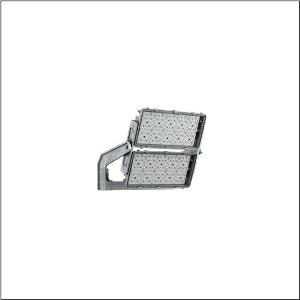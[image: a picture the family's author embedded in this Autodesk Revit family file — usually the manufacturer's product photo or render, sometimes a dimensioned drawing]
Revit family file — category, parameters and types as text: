
# Revit family: floodlight_fl_11_maxi_remote___rs12_5xa779514m01ba_3a09
name_source: partatom
category: Lighting Fixtures
units: mm (PartAtom-declared; Revit-internal decimal feet)

## family parameters
Cut with Voids When Loaded = No
Host = Face
Light Source = No
Part Type = Normal
Room Calculation Point = No
Round Connector Dimension = Use Diameter
Shared = No

## types (1)
- --- (1 x LED, 76660 lm, 707.9 W, 5700K)
    Apparent Load = 708 VA
    CIE Flux Codes = 79 92 99 100 100
    Color Rendering = 90
    Color Temperature = 5700K
    Default Elevation = 1800 mm
    Description = Floodlight FL 11  maxi  Remote floodlight; light control with lens of PMMA; cover panel of toughened safety glass, transparent; light distribution: RS12, rotationally symmetric direct distribution, LEDcolour temperature: 5700K, rated luminous flux: 76.660lm, colour rendering: CRI > 90, light colour: 957; luminous efficacy: 108lm/W; brightness control: DMX+RDM; with terminal, 8-pole, max. 2.5mm², mains connection: 220..240V/380..400V AC, 50/60Hz, surge voltage resistance: line to ground: 10kV, ECG replaceable separately, LED unit replaceable without ESD environment, dustproof LED module, dimming range 10..100%; 708W floodlight with 2x LED unit of diecast aluminium, coated grey; length: 713mm / width: 651mm / height: 338mm; mounting bracket, of diecast aluminium, uncoated, natural, equipment: Longlife, protection rating (complete): IP66; insulation class (complete): insulation class I (protective earthing); certification: CE, ENEC, VDE; ball protection: ball impact resistance with accessories, impact resistance: IK07; only for outdoor installations, rated ambient temperature 10°C, permissible operating ambient temperature: -40..+40°C, permissible storage temperature: -40..+85°C; packaging unit: 1 piece

Light Distribution: RS12
    Height = 320 mm
    Lamp = 1 x LED
    Lamp Light Flux = 76660 lm
    Lamp Power = 707.9 W
    Lamp count = 1
    Length = 712 mm
    Luminous efficacy = 108 lm/W
    Manufacturer = Siteco
    ModVariant = No
    Model = 5XA779514M01BA
    Mounting Place = Ceiling
    Mounting Type = Surface mounted
    Number of Poles = 1
    OnlyDefault = Yes
    Power Factor = 1
    Product Name = Floodlight FL 11 maxi Remote | RS12
    Product group = floodlight | ceiling mounted
    ProductGroupID = 303
    Protection Class = Protection class I
    Protection Degree = IP 66
    RLX_Detail_Level = 1
    RLX_Emergency_Light_Flux = 0 lm
    RLX_Emergency_Type = 0
    RLX_Emergency_Type_DB = No
    RlxData = <blob elided: 41041 chars, md5=bc130b86>
    Socket = socket
    Standby Power = 0 W
    System Light Flux = 76660 lm
    System Power = 708 W
    Type Comments = factory setting: luminous flux: 100 % | dim-lin: 254 | 740 mA
    Type Image = l_1006788.jpg
    URL = http://relux.com
    VarID = @adj_133497
    Voltage = 0 V
    Weight = 0.00 kg
    Width = 655 mm

## geometry (parser evidence)
native form markers: Blend x4, Sweep x12
no freeform markers — native parametric forms only
